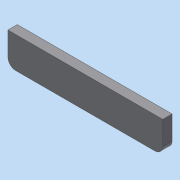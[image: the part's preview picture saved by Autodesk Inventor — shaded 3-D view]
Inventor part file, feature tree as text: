
AUTODESK INVENTOR PART (.ipt)
format: ipt  version: 2020 (Build 240168000, 168)  size: 84,480 bytes
history: native  units: mm
features: other x1, extrude x1
ambient origin geometry x8: Origin, YZ Plane, XZ Plane, XY Plane, X Axis, Y Axis, Z Axis, Center Point
bodies: Body1 (feature_tree)
feature tree (2):
  other  "實體1"
  extrude  "擠出1"  Depth=49.5mm
